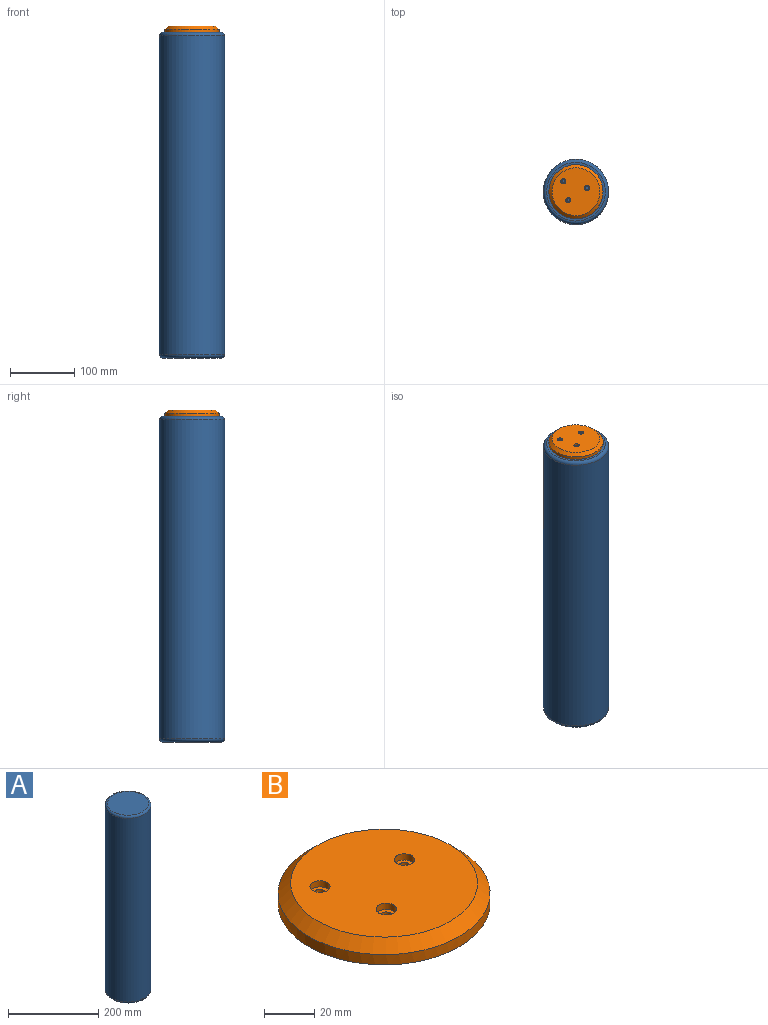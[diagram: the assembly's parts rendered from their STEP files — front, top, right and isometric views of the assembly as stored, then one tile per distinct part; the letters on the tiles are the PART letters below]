
ASSEMBLY  parts=2 mates=1
PART A: 5 faces, bbox 110x110x508 mm
  f0: cylinder r=50.8mm len=497.84mm, axis (0,0,-1), area 158903.5mm2, adj f3,f4
  f1: plane 91.44x91.44mm, normal (0,0,1), area 6566.9mm2, adj f4
  f2: plane 91.44x91.44mm, normal (0,0,-1), area 6566.9mm2, adj f3
  f3: torus R=45.72mm, axis (0,0,1), area 2454.4mm2, adj f0,f2
  f4: torus R=45.72mm, axis (0,0,1), area 2454.4mm2, adj f0,f1
PART B: 13 faces, bbox 84.5x84.5x10 mm
  f0: cylinder r=42.25mm len=84.51mm, axis (0,0,-1), area 1327.5mm2, adj f2,f12
  f1: plane 74.51x74.51mm, normal (0,0,1), area 4209.4mm2, adj f5,f8,f11,f12
  f2: plane 84.51x84.51mm, normal (0,0,-1), area 5561.4mm2, adj f0,f3,f6,f9
  f3: cylinder r=2.25mm len=7mm, axis (0,0,1), area 99mm2, adj f2,f4
  f4: plane 8x8mm, normal (0,0,1), area 34.4mm2, adj f3,f5
  f5: cylinder r=4mm len=8mm, axis (0,0,1), area 75.4mm2, adj f1,f4
  f6: cylinder r=2.25mm len=7mm, axis (0,0,1), area 99mm2, adj f2,f7
  f7: plane 8x8mm, normal (0,0,1), area 34.4mm2, adj f6,f8
  f8: cylinder r=4mm len=8mm, axis (0,0,1), area 75.4mm2, adj f1,f7
  f9: cylinder r=2.25mm len=7mm, axis (0,0,1), area 99mm2, adj f2,f10
  f10: plane 8x8mm, normal (0,0,1), area 34.4mm2, adj f9,f11
  f11: cylinder r=4mm len=8mm, axis (0,0,1), area 75.4mm2, adj f1,f10
  f12: cone r=37.25mm half-angle=45deg, axis (0,0,-1), area 1766.2mm2, adj f0,f1
PLACE A t=(-50.85,11.63,-544.12)mm
PLACE B t=(-50.85,11.63,-36.12)mm fixed
MATE cylindrical B.f0 <-> A.f0  axis (0,0,-1) through (-50.85,11.63,-33.62)mm
